# Revit family: Electronics_Communication_Talkaphone_AOR-32-Station-Analog-Command-Unit
name_source: partatom
category: Telephone Devices
units: mm (PartAtom-declared; Revit-internal decimal feet)

## family parameters
Cut with Voids When Loaded = No
Host = Face
Maintain Annotation Orientation = No
OmniClass Number = 23.37.27.17
Part Type = Normal
Room Calculation Point = No
Round Connector Dimension = Use Diameter
Shared = No

## types (1)
- 32-Station Analog Command Unit
    AC Input Rating = 115-230VAC, 50-60 Hz, 240W
    Apparent Load = 0 VA
    Approvals = Power Supply Approvals: UL 294 (6th Edition) listed, UL 603 listed, UL 1481 listed, ULC-S318 listed
    Assembly Code = D5030300
    Call Station Options = Indoor Flush Mount Model: AOR-CSE-FM, Indoor Surface Mount Model: AOR-CSE-SM
    Communication = Lighted phone with 12-button keypad receives and selectively originates calls
    Connection = Internal terminal block
    Connectivity = Supports one (1) analog phone line (PSTN line) per bank of 8-stations for off-site dialing (total of four (4) PSTN lines)
    Construction = 16 gauge, painted steel enclosure with polycarbonate windows
    Default Elevation = 48.00 in
    Depth = 6.00 in
    Description = THIS FULLY INTEGRATED COMMAND UNIT ACCOMMODATES UP TO 32 ADA-COMPLIANT AREA OF RESCUE STATIONS. THE UNIT’S STROBE/SOUNDER INDICATES AN INCOMING CALL, AND LED LIGHTS INDICATE THE CALLING LOCATION.
    Edition number = 1
    Environment = For indoor use
    Fault Monitoring = Activation of any AOR Station, opens/shorts on AOR Station cabling, 110VAC input power failure (primary power loss), low battery backup (low voltage detected), and system ground fault
    Fault Reset = Push button switch provided to temporarily silence while faults are corrected or to re-test/reset fault indicators after faults have been resolved
    Height = 43.60 in
    Keynote = 27 30 00
    Lighting = Strobe is rated at 15 candela, flashes once per second
    Manufacturer = Talkaphone
    Model = AOR-32
    Mounting = Surface mount or recess mount with optional trim ring (Model AOR-TR32). Strobe/sounder mounts to standard 4-inch square box.
    Number of Poles = 1
    Power Factor = 1
    Power Source = 120VAC, 1.0 A (max)
    Product Guid = b0aa63d3-a5a8-4e51-a462-b72029ba0090
    Product Material = Talkaphone - Steel - Black
    Product data url = https://www.bimobject.com
    Programming = Programming of the Analog Command Unit and Analog Stations can be carried out through the built-in phone via touch-tone commands. All programming is stored on non-volatile EEPROMs.
    Sound = Strobe/siren outputs 1 of 8 alerting sounds ranging from 90 to 100 dBA
    Supervision Relay = Activation of Any AOR Station: Contact closure (relay) output; Open/Short Fault on AOR Stations: Contact closure (relay) output; AC Input Power Failure: 24VDC output; Low Battery (Low Voltage Detected): Form C output; and System Ground Fault: Contact closure (relay) output.
    URL = https://www.talkaphone.com
    Voltage = 120 V
    Warranty = 5-year limited warranty
    Width = 14.50 in
    Wiring = One (1) twisted, shielded pair per station not to exceed 25 ohms resistance

## geometry (parser evidence)
native form markers: Sweep x2
no freeform markers — native parametric forms only
